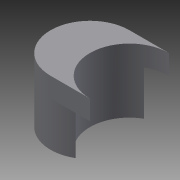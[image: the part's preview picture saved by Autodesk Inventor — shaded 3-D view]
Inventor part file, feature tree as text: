
AUTODESK INVENTOR PART (.ipt)
format: ipt  version: 2015 SP1 (Build 190203100, 203)  size: 90,112 bytes
history: native  units: mm
features: extrude x3, sketch x3
ambient origin geometry x8: Origin, YZ Plane, XZ Plane, XY Plane, X Axis, Y Axis, Z Axis, Center Point
bodies: Solid1 (feature_tree)
feature tree (6):
  extrude  "Extrusion1"  Depth=16.0mm
  extrude  "Extrusion2"  Depth=4.0mm TaperAngle=0.0deg
  extrude  "Extrusion3"  [1 undecoded]
  sketch  "Sketch1"  dims[d0=16.0mm d1=12.0mm]
  sketch  "Sketch2"  dims[d2=13.0mm d3=0.0mm d4=4.0mm d5=0.0mm]
  sketch  "Sketch3"  dims[d6=4.0mm d7=0.0mm]
note: 1 required parameter value undecoded (feature->parameter linkage not recoverable at this tier; creation-order binding heuristic only, values carry confidence <= 0.55)
